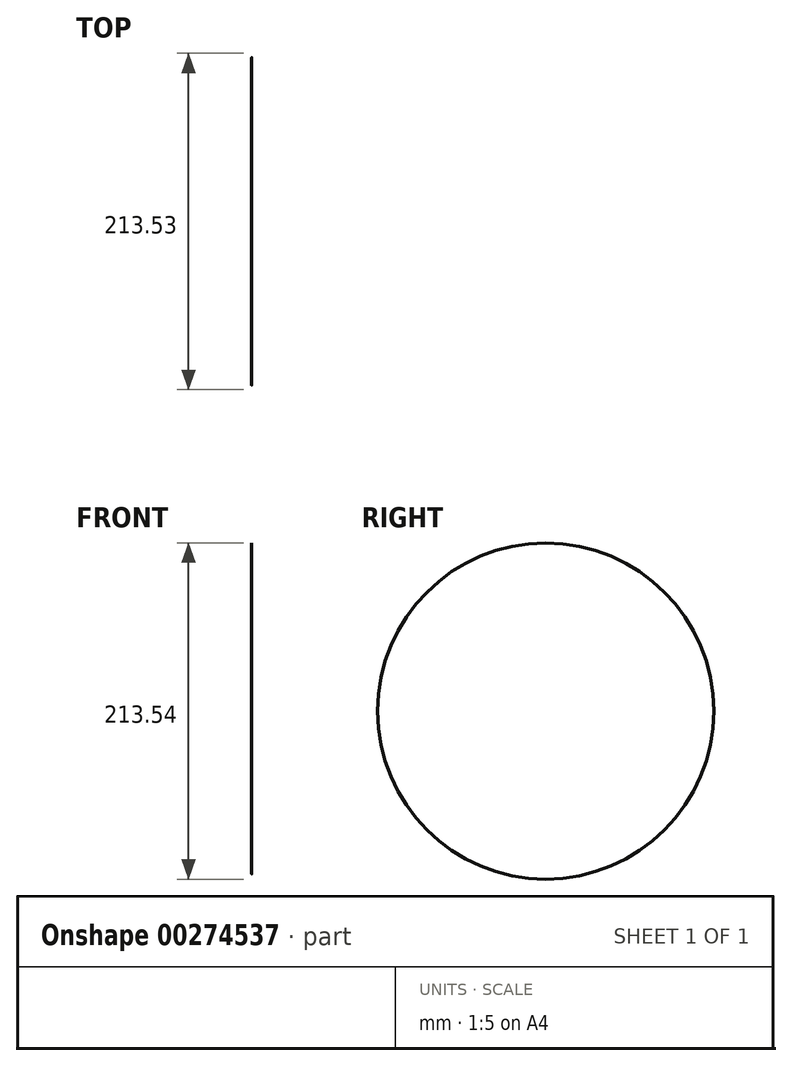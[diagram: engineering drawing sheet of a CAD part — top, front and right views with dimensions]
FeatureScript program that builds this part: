
annotation { "Feature Type Name" : "Feature", "Feature Type Description" : "" }
export const myFeature = defineFeature(function(context is Context, id is Id, definition is map)
    precondition{}
    {
        {
            var Q0;
            Q0=qCreatedBy(makeId("Top.planeOp"),FACE);
            var sketch = newSketch(context, id + "F0", { "sketchPlane" : qUnion([Q0])});
            skArc(sketch, "E0", {"start": v(0, -65.47) * mm, "mid": v(59.12, -28.13) * mm, "end": v(50.8, 41.3) * mm});
            skLineSegment(sketch, "E1", {"start": v(0, 41.3) * mm, "end": v(0, -65.47) * mm});
            skLineSegment(sketch, "E2", {"start": v(0, 41.3) * mm, "end": v(50.8, 41.3) * mm});
            skLineSegment(sketch, "E3", {"start": v(50.8, 41.3) * mm, "end": v(0, 41.3) * mm});
            skPoint(sketch, "E4.orphan", {"position": v(0, 65.47) * mm});
            skSolve(sketch);
        }
        {
            var Q0;
            Q0=makeQuery(id+"F0.imprint","IMPRINT",FACE,{"disambiguationData":[TD([[makeQuery(id+"F0.imprint","IMPRINT",EDGE,{"derivedFrom":sQuery(id+"F0.wireOp",EDGE,"E0")}),1.0]])]});
            var Q1;
            Q1=sQuery(id+"F0.wireOp",EDGE,"E1");
            var Q2;
            Q2=sQuery(id+"F0.wireOp",EDGE,"E3");
            revolve(context, id + "F1", {"bodyType" : ToolBodyType.SURFACE, "entities" : qUnion([Q0]), "surfaceEntities" : qUnion([Q1]), "axis" : qUnion([Q2]), "revolveType" : RevolveType.FULL});
        }
    });
